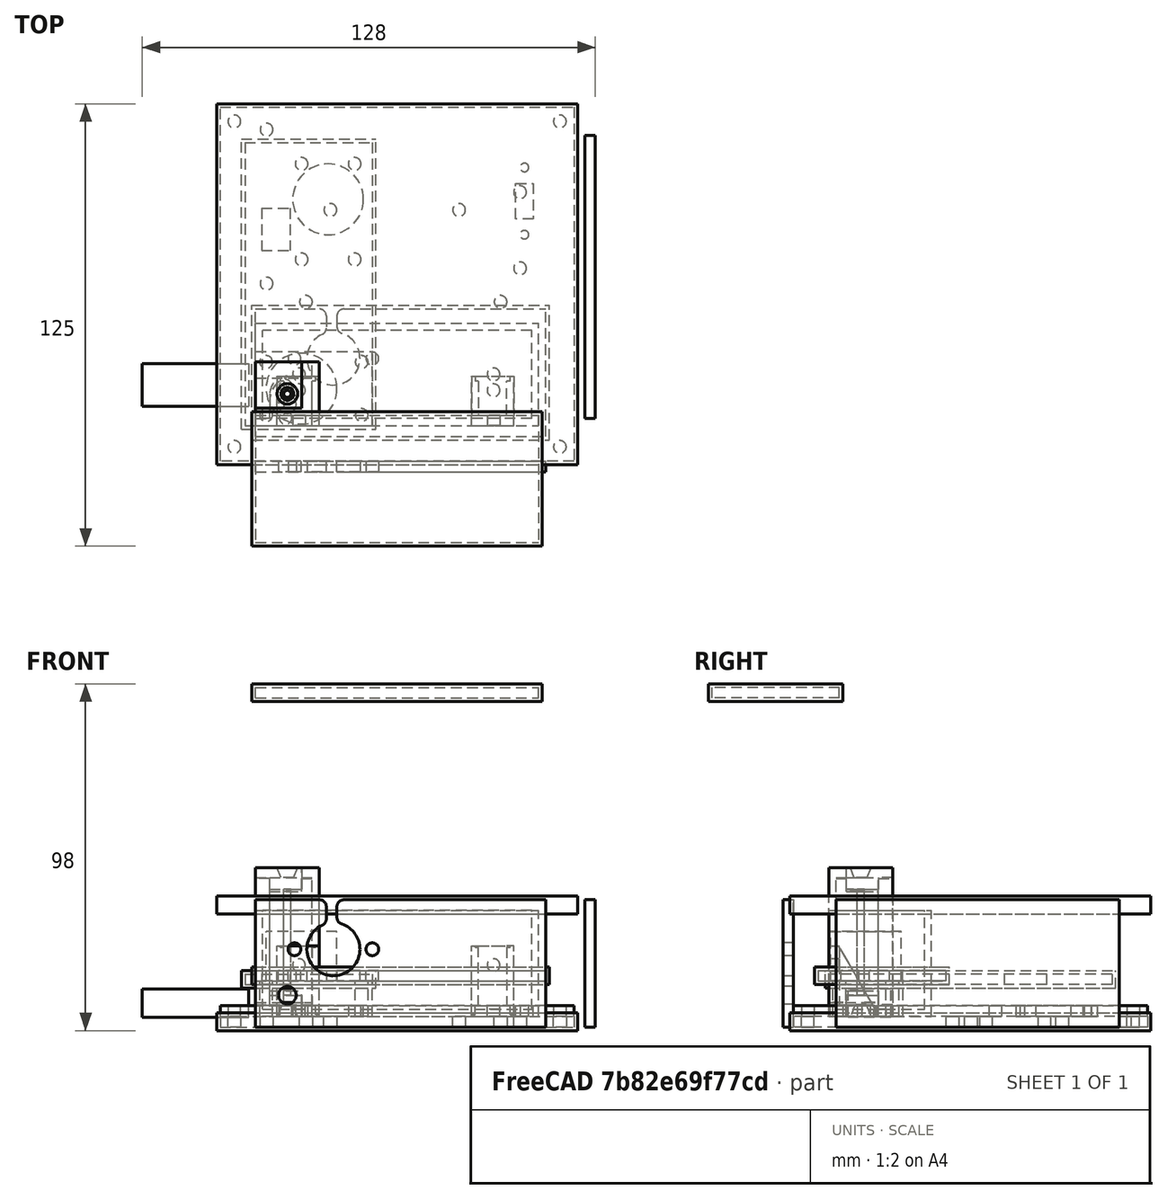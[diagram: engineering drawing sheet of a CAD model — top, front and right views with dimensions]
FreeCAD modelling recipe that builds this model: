
FCSTD DOCUMENT  (FreeCAD 0.19R)
Label: MQsensors
License: All rights reserved
LicenseURL: http://en.wikipedia.org/wiki/All_rights_reserved
objects: Part::Box×23, Part::FeaturePython×18, Path::FeaturePython×15, App::Part×14, Part::Cylinder×11, App::DocumentObjectGroup×10, Part::Cut×9, PartDesign::Body×8, Part::MultiFuse×7, PartDesign::FeatureBase×6, App::FeaturePython×5, Path::FeatureCompoundPython×5, Mesh::Feature×4, Part::Cone×4, Part::Fillet×4, Sketcher::SketchObject×3, PartDesign::Pad×3, PartDesign::Plane×1
note: 100 computed .brp shape members not serialized (recipe doc carries the construction recipe); baked Part::Feature solids carry a one-line shape summary decoded from their .brp

FEATURE [Mesh::Feature] esp8266_201
  Placement = pos=(25,43,0) rot=(0,0,1;0rad)
FEATURE [Mesh::Feature] step_down_12_1_8v  label="step_down_12-1.8v"
  Placement = pos=(63,62,-1e-16) rot=(0,0,1;4.71239rad)
FEATURE [Part::Box] Box  label="Cube"
  AttacherType = Attacher::AttachEngine3D
  Height = 30
  Length = 80
  Width = 29
FEATURE [Part::Box] Box001  label="Cube001"
  AttacherType = Attacher::AttachEngine3D
  Height = 30
  Length = 76
  Placement = pos=(2,2,2) rot=(0,0,-1;0rad)
  Width = 25
FEATURE [Part::Cylinder] Cylinder
  Angle = 360
  AttacherType = Attacher::AttachEngine3D
  Height = 50
  Placement = pos=(12.25,14.5,-10) rot=(0,0,1;0rad)
  Radius = 1.8
FEATURE [Part::FeaturePython] Array  # Draft array (typed FeaturePython)
  Angle = 360
  ArrayType = 0
  Axis = (0,0,1)
  Base = -> Cylinder
  Center = (0,0,0)
  Fuse = false
  IntervalAxis = (0,0,0)
  IntervalX = (55,0,0)
  IntervalY = (0,1,0)
  IntervalZ = (0,0,1)
  NumberPolar = 1
  NumberX = 2
  NumberY = 1
  NumberZ = 1
FEATURE [Part::MultiFuse] Fusion
  Shapes = -> [Box001,Array]
FEATURE [Part::Cut] Cut
  Base = -> Box
  Tool = -> Fusion
FEATURE [App::Part] Part  label="battery mockup"
  Group = -> [Box001,Box,Cut,Cylinder,Array,Fusion]
  Origin = -> Origin
  Placement = pos=(2,25,-5.6e-15) rot=(1,0,0;1.5708rad)
FEATURE [Part::Box] Box002  label="Cube002"
  AttacherType = Attacher::AttachEngine3D
  Height = 4
  Length = 16
  Width = 13.5
FEATURE [Part::Cylinder] Cylinder001
  Angle = 360
  AttacherType = Attacher::AttachEngine3D
  Height = 50
  Placement = pos=(8.5,2.25,-10) rot=(0,0,1;0rad)
  Radius = 1.8
FEATURE [Part::FeaturePython] Array001  # Draft array (typed FeaturePython)
  Angle = 360
  ArrayType = 0
  Axis = (0,0,1)
  Base = -> Cylinder001
  Center = (0,0,0)
  Fuse = false
  IntervalAxis = (0,0,0)
  IntervalX = (1,0,0)
  IntervalY = (0,9,0)
  IntervalZ = (0,0,1)
  NumberPolar = 1
  NumberX = 1
  NumberY = 2
  NumberZ = 1
FEATURE [Part::Box] Box003  label="Cube003"
  AttacherType = Attacher::AttachEngine3D
  Height = 10
  Length = 33
  Width = 21
FEATURE [Part::Cylinder] Cylinder002
  Angle = 360
  AttacherType = Attacher::AttachEngine3D
  Height = 50
  Placement = pos=(3,3,-10) rot=(0,0,1;0rad)
  Radius = 1.8
FEATURE [Part::FeaturePython] Array002  # Draft array (typed FeaturePython)
  Angle = 360
  ArrayType = 0
  Axis = (0,0,1)
  Base = -> Cylinder002
  Center = (0,0,0)
  Fuse = false
  IntervalAxis = (0,0,0)
  IntervalX = (27,0,0)
  IntervalY = (0,15,0)
  IntervalZ = (0,0,1)
  NumberPolar = 1
  NumberX = 2
  NumberY = 2
  NumberZ = 1
FEATURE [Part::Cut] Cut002
  Base = -> Box003
  Tool = -> Array002
FEATURE [Part::Cylinder] Cylinder003
  Angle = 360
  AttacherType = Attacher::AttachEngine3D
  Height = 14
  Placement = pos=(13,10.5,10) rot=(0,0,1;0rad)
  Radius = 10
FEATURE [App::Part] Part002  label="sensor mockup"
  Group = -> [Box003,Cylinder002,Array002,Cut002,Cylinder003]
  Origin = -> Origin002
  Placement = pos=(10,77,19) rot=(0,0,1;4.71239rad)
FEATURE [Mesh::Feature] switch_mockup_plate
  Placement = pos=(75.3409,-19.717,22) rot=(0,0,-1;4.71239rad)
FEATURE [Part::Box] Box004  label="Cube004"
  AttacherType = Attacher::AttachEngine3D
  Height = 20
  Length = 10
  Placement = pos=(7,0,0) rot=(0,0,1;0rad)
  Width = 3
FEATURE [Part::Box] Box005  label="Cube005"
  AttacherType = Attacher::AttachEngine3D
  Height = 3
  Length = 10
  Placement = pos=(7,2,0) rot=(0,0,1;0rad)
  Width = 12
FEATURE [Part::Cylinder] Cylinder004
  Angle = 360
  AttacherType = Attacher::AttachEngine3D
  Height = 40
  Placement = pos=(12.25,10,14.5) rot=(1,0,0;1.5708rad)
  Radius = 1.8
FEATURE [Part::Cylinder] Cylinder005
  Angle = 360
  AttacherType = Attacher::AttachEngine3D
  Height = 50
  Placement = pos=(12.25,10,-21) rot=(0,0,1;0rad)
  Radius = 1.8
FEATURE [Part::MultiFuse] Fusion002
  Shapes = -> [Cylinder005,Cylinder004]
FEATURE [Part::Box] Box006  label="Cube006"
  AttacherType = Attacher::AttachEngine3D
  Height = 20
  Length = 2
  Placement = pos=(6,0,0) rot=(0,0,1;0rad)
  Width = 14
FEATURE [Part::Box] Box007  label="Cube007"
  AttacherType = Attacher::AttachEngine3D
  Height = 40
  Length = 2
  Placement = pos=(6,16.3978,-3.62848) rot=(1,0,0;0.523599rad)
  Width = 20
FEATURE [Part::Cut] Cut004
  Base = -> Box006
  Tool = -> Box007
FEATURE [Part::FeaturePython] Array004  # Draft array (typed FeaturePython)
  Angle = 360
  ArrayType = 0
  Axis = (0,0,1)
  Base = -> Cut004
  Center = (0,0,0)
  Fuse = false
  IntervalAxis = (0,0,0)
  IntervalX = (10,0,0)
  IntervalY = (0,1,0)
  IntervalZ = (0,0,1)
  NumberPolar = 1
  NumberX = 2
  NumberY = 0
  NumberZ = 1
FEATURE [Part::MultiFuse] Fusion001
  Shapes = -> [Box004,Box005,Array004]
FEATURE [Part::Cut] Cut003
  Base = -> Fusion001
  Tool = -> Fusion002
FEATURE [Part::FeaturePython] Array003  # Draft array (typed FeaturePython)
  Angle = 360
  ArrayType = 0
  Axis = (0,0,1)
  Base = -> Cut003
  Center = (0,0,0)
  Fuse = false
  IntervalAxis = (0,0,0)
  IntervalX = (55,0,0)
  IntervalY = (0,1,0)
  IntervalZ = (0,0,1)
  NumberPolar = 1
  NumberX = 2
  NumberY = 1
  NumberZ = 1
FEATURE [App::Part] Part003  label="battery holder brackets"
  Group = -> [Box005,Array003,Box004,Fusion001,Cylinder004,Cylinder005,Fusion002,Cut003,Box006,Box007,Cut004,Array004]
  Origin = -> Origin003
  Placement = pos=(2,25,0) rot=(0,0,1;0rad)
FEATURE [PartDesign::Plane] DatumPlane
  Length = 138
  MapMode = 5
  ResizeMode = 0
  Support = -> [XY_Plane004]
  Width = 138
FEATURE [Sketcher::SketchObject] Sketch
  FullyConstrained = false
  MapMode = 5
  Support = -> [DatumPlane]
  sketch-geometry (16):
    g0: LineSegment StartX=-10 StartY=90 StartZ=0 EndX=90 EndY=90 EndZ=0
    g1: LineSegment StartX=90 StartY=90 StartZ=0 EndX=90 EndY=-10 EndZ=0
    g2: LineSegment StartX=90 StartY=-10 StartZ=0 EndX=-10 EndY=-10 EndZ=0
    g3: LineSegment StartX=-10 StartY=-10 StartZ=0 EndX=-10 EndY=90 EndZ=0
    g4: Circle CenterX=3.12 CenterY=83.7 CenterZ=0 NormalX=0 NormalY=0 NormalZ=1 AngleXU=0 Radius=1.8
    g5: Circle CenterX=3.12 CenterY=40.2 CenterZ=0 NormalX=0 NormalY=0 NormalZ=1 AngleXU=0 Radius=1.8
    g6: Circle CenterX=14.25 CenterY=35 CenterZ=0 NormalX=0 NormalY=0 NormalZ=1 AngleXU=0 Radius=1.8
    g7: Circle CenterX=69.25 CenterY=35 CenterZ=0 NormalX=0 NormalY=0 NormalZ=1 AngleXU=0 Radius=1.8
    g8: Circle CenterX=74.74 CenterY=66 CenterZ=0 NormalX=0 NormalY=0 NormalZ=1 AngleXU=0 Radius=1.8
    g9: Circle CenterX=74.74 CenterY=44.5 CenterZ=0 NormalX=0 NormalY=0 NormalZ=1 AngleXU=0 Radius=1.8
    g10: Circle CenterX=21.13 CenterY=61 CenterZ=0 NormalX=0 NormalY=0 NormalZ=1 AngleXU=0 Radius=1.8
    g11: Circle CenterX=57.53 CenterY=61 CenterZ=0 NormalX=0 NormalY=0 NormalZ=1 AngleXU=0 Radius=1.8
    g12: Circle CenterX=-6 CenterY=86 CenterZ=0 NormalX=0 NormalY=0 NormalZ=1 AngleXU=0 Radius=1.8
    g13: Circle CenterX=86 CenterY=86 CenterZ=0 NormalX=0 NormalY=0 NormalZ=1 AngleXU=0 Radius=1.8
    g14: Circle CenterX=-6 CenterY=-6 CenterZ=0 NormalX=0 NormalY=0 NormalZ=1 AngleXU=0 Radius=1.8
    g15: Circle CenterX=86 CenterY=-6 CenterZ=0 NormalX=0 NormalY=0 NormalZ=1 AngleXU=0 Radius=1.8
  constraints (48):
    c: Coincident(g0,g1)
    c: Coincident(g1,g2)
    c: Coincident(g2,g3)
    c: Coincident(g3,g0)
    c: Horizontal(g0)
    c: Horizontal(g2)
    c: Vertical(g1)
    c: Vertical(g3)
    c: Equal(g7,g6)
    c: Equal(g11,g10)
    c: Radius(g11) = 1.8
    c: DistanceY(g10,g11) = 0
    c: DistanceX(g10,g11) = 36.4
    c: Equal(g4,g5)
    c: DistanceY(g6,g7) = 0
    c: DistanceX(g6,g7) = 55
    c: Radius(g6) = 1.8
    c: Equal(g8,g9)
    c: Radius(g8) = 1.8
    c: DistanceX(g8,g9) = 0
    c: DistanceY(g9,g8) = 21.5
    c: DistanceY(g1,g1) = 100
    c: DistanceX(g0,g0) = 100
    c: DistanceX(g2,g-1) = 10
    c: DistanceY(g2,g-1) = 10
    c: DistanceY(g-1,g6) = 35
    c: Radius(g12) = 1.8
    c: Equal(g12,g13)
    c: Equal(g13,g15)
    c: Equal(g15,g14)
    c: DistanceX(g2,g14) = 4
    c: DistanceY(g2,g14) = 4
    c: DistanceY(g15,g14) = 0
    c: DistanceX(g15,g1) = 4
    c: DistanceX(g15,g13) = 0
    c: DistanceY(g13,g0) = 4
    c: DistanceY(g13,g12) = 0
    c: DistanceX(g12,g14) = 0
    c: DistanceY(g-1,g10) = 61
    c: DistanceY(g-1,g9) = 44.5
    c: DistanceX(g-1,g10) = 21.13
    c: DistanceX(g4,g5) = 0
    c: DistanceY(g5,g4) = 43.5
    c: DistanceX(g-1,g5) = 3.12
    c: DistanceY(g-1,g5) = 40.2
    c: DistanceX(g-1,g9) = 74.74
    c: Radius(g4) = 1.8
    c: DistanceX(g-1,g6) = 14.25
FEATURE [Sketcher::SketchObject] Sketch001
  FullyConstrained = false
  sketch-geometry (19):
    g0: LineSegment StartX=-10 StartY=90 StartZ=0 EndX=90 EndY=90 EndZ=0
    g1: LineSegment StartX=90 StartY=90 StartZ=0 EndX=90 EndY=-10 EndZ=0
    g2: LineSegment StartX=90 StartY=-10 StartZ=0 EndX=-10 EndY=-10 EndZ=0
    g3: LineSegment StartX=-10 StartY=-10 StartZ=0 EndX=-10 EndY=90 EndZ=0
    g4: Circle CenterX=76 CenterY=73 CenterZ=0 NormalX=0 NormalY=0 NormalZ=1 AngleXU=0 Radius=1.2
    g5: Circle CenterX=76 CenterY=54 CenterZ=0 NormalX=0 NormalY=0 NormalZ=1 AngleXU=0 Radius=1.2
    g6: Circle CenterX=28 CenterY=47 CenterZ=0 NormalX=0 NormalY=0 NormalZ=1 AngleXU=0 Radius=1.8
    g7: Circle CenterX=13 CenterY=47 CenterZ=0 NormalX=0 NormalY=0 NormalZ=1 AngleXU=0 Radius=1.8
    g8: Circle CenterX=13 CenterY=74 CenterZ=0 NormalX=0 NormalY=0 NormalZ=1 AngleXU=0 Radius=1.8
    g9: Circle CenterX=28 CenterY=74 CenterZ=0 NormalX=0 NormalY=0 NormalZ=1 AngleXU=0 Radius=1.8
    g10: Circle CenterX=20.5 CenterY=64 CenterZ=0 NormalX=0 NormalY=0 NormalZ=1 AngleXU=0 Radius=10
    g11: LineSegment StartX=78.5 StartY=58.5 StartZ=0 EndX=73.5 EndY=58.5 EndZ=0
    g12: LineSegment StartX=73.5 StartY=58.5 StartZ=0 EndX=73.5 EndY=68.5 EndZ=0
    g13: LineSegment StartX=73.5 StartY=68.5 StartZ=0 EndX=78.5 EndY=68.5 EndZ=0
    g14: LineSegment StartX=78.5 StartY=68.5 StartZ=0 EndX=78.5 EndY=58.5 EndZ=0
    g15: Circle CenterX=-6 CenterY=86 CenterZ=0 NormalX=0 NormalY=0 NormalZ=1 AngleXU=0 Radius=1.8
    g16: Circle CenterX=86 CenterY=86 CenterZ=0 NormalX=0 NormalY=0 NormalZ=1 AngleXU=0 Radius=1.8
    g17: Circle CenterX=-6 CenterY=-6 CenterZ=0 NormalX=0 NormalY=0 NormalZ=1 AngleXU=0 Radius=1.8
    g18: Circle CenterX=86 CenterY=-6 CenterZ=0 NormalX=0 NormalY=0 NormalZ=1 AngleXU=0 Radius=1.8
  constraints (57):
    c: Coincident(g0,g1)
    c: Coincident(g1,g2)
    c: Coincident(g2,g3)
    c: Coincident(g3,g0)
    c: Horizontal(g0)
    c: Horizontal(g2)
    c: Vertical(g1)
    c: Vertical(g3)
    c: Coincident(g11,g12)
    c: Coincident(g12,g13)
    c: Coincident(g13,g14)
    c: Coincident(g14,g11)
    c: Horizontal(g11)
    c: Horizontal(g13)
    c: Vertical(g12)
    c: Vertical(g14)
    c: DistanceY(g8,g9) = 0
    c: DistanceY(g6,g7) = 0
    c: DistanceX(g9,g6) = 0
    c: Radius(g7) = 1.8
    c: Equal(g7,g6)
    c: Equal(g6,g9)
    c: Equal(g9,g8)
    c: DistanceY(g6,g9) = 27
    c: DistanceX(g7,g6) = 15
    c: Radius(g5) = 1.2
    c: Equal(g4,g5)
    c: DistanceY(g1,g1) = 100
    c: DistanceX(g0,g0) = 100
    c: DistanceX(g11,g11) = 5
    c: DistanceY(g12,g12) = 10
    c: DistanceX(g2,g-1) = 10
    c: DistanceY(g2,g-1) = 10
    c: Radius(g10) = 10
    c: DistanceX(g7,g10) = 7.5
    c: DistanceY(g10,g8) = 10
    c: DistanceX(g7,g8) = 0
    c: Radius(g15) = 1.8
    c: Equal(g15,g16)
    c: Equal(g16,g18)
    c: Equal(g18,g17)
    c: DistanceX(g2,g17) = 4
    c: DistanceY(g2,g17) = 4
    c: DistanceY(g18,g17) = 0
    c: DistanceX(g18,g1) = 4
    c: DistanceX(g18,g16) = 0
    c: DistanceY(g16,g0) = 4
    c: DistanceY(g16,g15) = 0
    c: DistanceX(g15,g17) = 0
    c: DistanceX(g-1,g7) = 13
    c: DistanceX(g5,g4) = 0
    c: DistanceY(g5,g4) = 19
    c: DistanceX(g12,g4) = 2.5
    c: DistanceY(g12,g4) = 4.5
    c: DistanceX(g17,g5) = 82
    c: DistanceY(g17,g5) = 60
    c: DistanceY(g-1,g7) = 47
FEATURE [PartDesign::Pad] Pad001
  AllowMultiFace = false
  Direction = (1,1,1)
  Length = 3
  Length2 = 100
  Profile = -> Sketch001
  Type = 0
FEATURE [PartDesign::Body] Body001  label="top plate"
  Group = -> [Sketch001,Pad001]
  Origin = -> Origin007
  Tip = -> Pad001
FEATURE [App::Part] Part005  label="top plate part"
  Group = -> [Body001]
  Origin = -> Origin006
  Placement = pos=(0,0,30) rot=(0,0,1;0rad)
FEATURE [PartDesign::Pad] Pad
  AllowMultiFace = false
  Direction = (1,1,1)
  Length = 3
  Length2 = 100
  Profile = -> Sketch
  Reversed = true
  Type = 0
FEATURE [PartDesign::Body] Body  label="bottom plate"
  Group = -> [DatumPlane,Sketch,Pad]
  Origin = -> Origin004
  Tip = -> Pad
FEATURE [App::Part] Part004  label="bottom plate part"
  Group = -> [Body]
  Origin = -> Origin005
FEATURE [Mesh::Feature] lion_manager
  Placement = pos=(0,0,0) rot=(0,0,1;1.5708rad)
FEATURE [Part::Cut] Cut001
  Base = -> Box002
  Tool = -> Array001
FEATURE [App::Part] Part001  label="micro usb mockup"
  Group = -> [Box002,Cylinder001,Array001,Cut001]
  Origin = -> Origin001
  Placement = pos=(63,87,0) rot=(0,0,1;4.71239rad)
FEATURE [App::FeaturePython] SetupSheet  # Path/CAM operation (typed FeaturePython)
  ClearanceHeightExpression = OpStockZMax+SetupSheet.ClearanceHeightOffset
  ClearanceHeightOffset = 0
  CoolantMode = 0
  CoolantModes = None | Flood | Mist
  FinalDepthExpression = OpFinalDepth
  HorizRapid = 10
  SafeHeightExpression = OpStockZMax+SetupSheet.SafeHeightOffset
  SafeHeightOffset = 0
  StartDepthExpression = OpStartDepth
  StepDownExpression = OpToolDiameter
  VertRapid = 10
FEATURE [Part::FeaturePython] Clone  label="Model-bottom plate part"  # Draft clone (typed FeaturePython)
  AttacherType = Attacher::AttachEngine3D
  Fuse = false
  Objects = -> [Part004]
  PathResource = Model
  Scale = (1,1,1)
FEATURE [App::DocumentObjectGroup] Model
  Group = -> [Clone]
FEATURE [Part::FeaturePython] Stock  # WARN: FeaturePython — macro-defined, semantics opaque (R4)
  Base = -> Model
  ExtXneg = 1
  ExtXpos = 1
  ExtYneg = 1
  ExtYpos = 1
  ExtZneg = 1
  ExtZpos = 1
  Placement = pos=(-10,-10,-3) rot=(0,0,1;0rad)
  StockType = FromBase
FEATURE [Path::FeaturePython] T3__laser  label="T3: laser"  # Path/CAM operation (typed FeaturePython)
  HorizFeed = 1
  HorizRapid = 10
  SpindleDir = 0
  SpindleSpeed = 1000
  ToolNumber = 3
  VertFeed = 1
  VertRapid = 10
  expr: HorizRapid = SetupSheet.HorizRapid
  expr: VertRapid = SetupSheet.VertRapid
FEATURE [Path::FeaturePython] Engrave  # Path/CAM operation (typed FeaturePython)
  Active = true
  Base = -> [Clone]
  ClearanceHeight = 1
  FinalDepth = 0
  OpFinalDepth = -0.2
  OpStartDepth = 0
  OpStockZMax = 1
  OpStockZMin = -4
  OpToolDiameter = 0.2
  SafeHeight = 1
  StartDepth = 0
  StartVertex = 0
  StepDown = 0.2
  ToolController = -> T3__laser
  expr: ClearanceHeight = OpStockZMax + SetupSheet.ClearanceHeightOffset
  expr: SafeHeight = OpStockZMax + SetupSheet.SafeHeightOffset
  expr: StepDown = OpToolDiameter
  expr: StartDepth = OpStartDepth
FEATURE [Path::FeatureCompoundPython] Operations  # Path/CAM operation (typed FeaturePython)
  Group = -> [Engrave]
  UsePlacements = false
FEATURE [App::FeaturePython] SetupSheet001  # Path/CAM operation (typed FeaturePython)
  ClearanceHeightExpression = OpStockZMax+SetupSheet001.ClearanceHeightOffset
  ClearanceHeightOffset = 0
  CoolantMode = 0
  CoolantModes = None | Flood | Mist
  FinalDepthExpression = OpFinalDepth
  HorizRapid = 10
  SafeHeightExpression = OpStockZMax+SetupSheet001.SafeHeightOffset
  SafeHeightOffset = 0
  StartDepthExpression = OpStartDepth
  StepDownExpression = OpToolDiameter
  VertRapid = 10
FEATURE [Part::FeaturePython] Clone001  label="Model-top plate part"  # Draft clone (typed FeaturePython)
  AttacherType = Attacher::AttachEngine3D
  Fuse = false
  Objects = -> [Part005]
  PathResource = Model
  Scale = (1,1,1)
FEATURE [App::DocumentObjectGroup] Model001
  Group = -> [Clone001]
FEATURE [Part::FeaturePython] Stock001  # WARN: FeaturePython — macro-defined, semantics opaque (R4)
  Base = -> Model001
  ExtXneg = 1
  ExtXpos = 1
  ExtYneg = 1
  ExtYpos = 1
  ExtZneg = 1
  ExtZpos = 1
  Placement = pos=(-10,-10,30) rot=(0,0,1;0rad)
  StockType = FromBase
FEATURE [Path::FeaturePython] T3__laser001  label="T3: laser001"  # Path/CAM operation (typed FeaturePython)
  HorizFeed = 0.6
  HorizRapid = 10
  SpindleDir = 0
  SpindleSpeed = 1000
  ToolNumber = 3
  VertFeed = 0.6
  VertRapid = 10
  expr: HorizRapid = SetupSheet001.HorizRapid
  expr: VertRapid = SetupSheet001.VertRapid
FEATURE [Path::FeaturePython] Engrave001  # Path/CAM operation (typed FeaturePython)
  Active = true
  Base = -> [Clone001]
  ClearanceHeight = 34
  FinalDepth = 0
  OpFinalDepth = 2.8
  OpStartDepth = 3
  OpStockZMax = 34
  OpStockZMin = 29
  OpToolDiameter = 0.2
  SafeHeight = 34
  StartDepth = 0
  StartVertex = 0
  StepDown = 0.2
  ToolController = -> T3__laser001
  expr: ClearanceHeight = OpStockZMax + SetupSheet001.ClearanceHeightOffset
  expr: SafeHeight = OpStockZMax + SetupSheet001.SafeHeightOffset
  expr: StepDown = OpToolDiameter
FEATURE [Path::FeatureCompoundPython] Operations001  # Path/CAM operation (typed FeaturePython)
  Group = -> [Engrave001]
  UsePlacements = false
FEATURE [Part::Box] Box008  label="Cube008"
  AttacherType = Attacher::AttachEngine3D
  Height = 36
  Length = 82
  Placement = pos=(0,-13,-3) rot=(0,0,1;0rad)
  Width = 3
FEATURE [Part::Box] Box009  label="plane wall cube"
  AttacherType = Attacher::AttachEngine3D
  Height = 36
  Length = 80
  Placement = pos=(0,90,-3) rot=(0,0,1;0rad)
  Width = 3
FEATURE [Part::Box] Box010  label="Cube010"
  AttacherType = Attacher::AttachEngine3D
  Height = 42
  Length = 18
  Width = 18
FEATURE [Part::Box] Box011  label="Cube011"
  AttacherType = Attacher::AttachEngine3D
  Height = 4
  Length = 18
  Placement = pos=(-5,5,3.3) rot=(0,0,1;0rad)
  Width = 18
FEATURE [Part::Box] Box012  label="Cube012"
  AttacherType = Attacher::AttachEngine3D
  Height = 36
  Length = 18
  Placement = pos=(-14,2,3.3) rot=(0,0,1;0rad)
  Width = 18
FEATURE [Part::Box] Box013  label="Cube013"
  AttacherType = Attacher::AttachEngine3D
  Height = 36
  Length = 18
  Placement = pos=(-2,14,3.3) rot=(0,0,1;0rad)
  Width = 18
FEATURE [Part::Cylinder] Cylinder006
  Angle = 360
  AttacherType = Attacher::AttachEngine3D
  Height = 70
  Placement = pos=(9,9,-17) rot=(0,0,1;0rad)
  Radius = 1
FEATURE [Part::FeaturePython] Array005  # Draft array (typed FeaturePython)
  Angle = 360
  ArrayType = 0
  Axis = (0,0,1)
  Base = -> Box011
  Center = (0,0,0)
  Fuse = false
  IntervalAxis = (0,0,0)
  IntervalX = (1,0,0)
  IntervalY = (0,1,0)
  IntervalZ = (0,0,32)
  NumberPolar = 1
  NumberX = 1
  NumberY = 1
  NumberZ = 2
FEATURE [Part::Cone] Cone
  Angle = 360
  AttacherType = Attacher::AttachEngine3D
  Height = 3.5
  Placement = pos=(9,9,0) rot=(0,0,1;0rad)
  Radius1 = 2.9
  Radius2 = 1.5
FEATURE [Part::Cone] Cone001
  Angle = 360
  AttacherType = Attacher::AttachEngine3D
  Height = 3.5
  Placement = pos=(9,9,38.5) rot=(0,0,1;0rad)
  Radius1 = 1.5
  Radius2 = 2.9
FEATURE [Part::MultiFuse] Fusion003
  Shapes = -> [Box012,Box013,Cylinder006,Array005,Cone,Cone001]
FEATURE [Part::Cut] Cut005
  Base = -> Box010
  Tool = -> Fusion003
FEATURE [Part::Fillet] Fillet
  Base = -> Cut005
  Edges = 1 edges r=5: [Edge58]
FEATURE [App::Part] Part007  label="corner part"
  Group = -> [Box010,Box012,Box013,Fusion003,Cut005,Cylinder006,Box011,Array005,Cone,Cone001,Fillet]
  Origin = -> Origin009
  Placement = pos=(77,-15,-6.3) rot=(0,0,1;0rad)
FEATURE [PartDesign::FeatureBase] Clone002
  BaseFeature = -> Fillet
FEATURE [PartDesign::Body] Body002  label="corner clone"
  BaseFeature = -> Fillet
  Group = -> [Clone002]
  Origin = -> Origin010
  Tip = -> Clone002
FEATURE [App::Part] Part008  label="corner clone part"
  Group = -> [Body002]
  Origin = -> Origin011
  Placement = pos=(-15,3,-6) rot=(0,0,1;4.71239rad)
FEATURE [Part::Cylinder] Cylinder007
  Angle = 360
  AttacherType = Attacher::AttachEngine3D
  Height = 23
  Radius = 7.5
FEATURE [Part::Cylinder] Cylinder008
  Angle = 360
  AttacherType = Attacher::AttachEngine3D
  Height = 10
  Placement = pos=(-11,0,0) rot=(0,0,1;0rad)
  Radius = 1.8
FEATURE [Part::FeaturePython] Array006  # Draft array (typed FeaturePython)
  Angle = 360
  ArrayType = 0
  Axis = (0,0,1)
  Base = -> Cylinder008
  Center = (0,0,0)
  Fuse = false
  IntervalAxis = (0,0,0)
  IntervalX = (22,0,0)
  IntervalY = (0,1,0)
  IntervalZ = (0,0,1)
  NumberPolar = 1
  NumberX = 2
  NumberY = 0
  NumberZ = 1
FEATURE [Part::MultiFuse] Fusion004  label="tape recorder socket mockup"
  Shapes = -> [Cylinder007,Array006]
FEATURE [App::Part] Part009  label="tape recorder socket mockup part"
  Group = -> [Array006,Cylinder008,Cylinder007,Fusion004]
  Origin = -> Origin012
FEATURE [PartDesign::FeatureBase] Clone003  label="tape recorder socket clone"
  BaseFeature = -> Fusion004
  Placement = pos=(22,-4,19) rot=(1,0,0;1.5708rad)
FEATURE [Part::Cylinder] Cylinder009  label="led hole"
  Angle = 360
  AttacherType = Attacher::AttachEngine3D
  Height = 50
  Placement = pos=(0,0,0) rot=(1,0,0;1.5708rad)
  Radius = 2.5
FEATURE [App::Part] Part010  label="led mockup part"
  Origin = -> Origin014
FEATURE [PartDesign::FeatureBase] Clone004
  BaseFeature = -> Cylinder009
  Placement = pos=(0,0,0) rot=(1,0,0;1.5708rad)
FEATURE [PartDesign::Body] Body004  label="led hole clone body"
  BaseFeature = -> Cylinder009
  Group = -> [Clone004]
  Origin = -> Origin015
  Placement = pos=(9,16,6) rot=(0,0,1;0rad)
  Tip = -> Clone004
FEATURE [Part::Box] Box014  label="Cube014"
  AttacherType = Attacher::AttachEngine3D
  Height = 42
  Length = 18
  Width = 18
FEATURE [Part::Box] Box015  label="Cube015"
  AttacherType = Attacher::AttachEngine3D
  Height = 6
  Length = 18
  Placement = pos=(-5,5,0) rot=(0,0,1;0rad)
  Width = 18
FEATURE [Part::Box] Box016  label="Cube016"
  AttacherType = Attacher::AttachEngine3D
  Height = 36
  Length = 18
  Placement = pos=(-14,2,3) rot=(0,0,1;0rad)
  Width = 18
FEATURE [Part::Box] Box017  label="Cube017"
  AttacherType = Attacher::AttachEngine3D
  Height = 36
  Length = 18
  Placement = pos=(-2,14,3) rot=(0,0,1;0rad)
  Width = 18
FEATURE [Part::Cylinder] Cylinder010
  Angle = 360
  AttacherType = Attacher::AttachEngine3D
  Height = 70
  Placement = pos=(9,9,-17) rot=(0,0,1;0rad)
  Radius = 1
FEATURE [Part::FeaturePython] Array007  # Draft array (typed FeaturePython)
  Angle = 360
  ArrayType = 0
  Axis = (0,0,1)
  Base = -> Box015
  Center = (0,0,0)
  Fuse = false
  IntervalAxis = (0,0,0)
  IntervalX = (1,0,0)
  IntervalY = (0,1,0)
  IntervalZ = (0,0,36)
  NumberPolar = 1
  NumberX = 1
  NumberY = 1
  NumberZ = 2
FEATURE [Part::Cone] Cone002
  Angle = 360
  AttacherType = Attacher::AttachEngine3D
  Height = 3.5
  Placement = pos=(9,9,0) rot=(0,0,1;0rad)
  Radius1 = 2.9
  Radius2 = 1.5
FEATURE [Part::Cone] Cone003
  Angle = 360
  AttacherType = Attacher::AttachEngine3D
  Height = 3.5
  Placement = pos=(9,9,38.5) rot=(0,0,1;0rad)
  Radius1 = 1.5
  Radius2 = 2.9
FEATURE [Part::MultiFuse] Fusion006
  Shapes = -> [Box016,Box017,Cylinder010,Array007,Cone002,Cone003]
FEATURE [Part::Cut] Cut007
  Base = -> Box014
  Tool = -> Fusion006
FEATURE [Part::Fillet] Fillet001
  Base = -> Cut007
  Edges = 1 edges r=7: [Edge45]
FEATURE [App::Part] Part011  label="corner part v2"
  Group = -> [Box014,Box016,Box017,Fusion006,Cut007,Cylinder010,Box015,Array007,Cone002,Cone003,Fillet001]
  Origin = -> Origin016
  Placement = pos=(77,-15,-6) rot=(0,0,1;0rad)
FEATURE [Part::Box] Box018  label="plane wall cube 1"
  AttacherType = Attacher::AttachEngine3D
  Height = 36
  Length = 80
  Placement = pos=(93,82,-3) rot=(0,0,-1;1.5708rad)
  Width = 3
FEATURE [Part::Box] Box019  label="Cube019"
  AttacherType = Attacher::AttachEngine3D
  Height = 36
  Length = 80
  Placement = pos=(0,0,0) rot=(0,0,-1;1.5708rad)
  Width = 3
FEATURE [Part::Box] Box020  label="micro usb hole"
  AttacherType = Attacher::AttachEngine3D
  Height = 8
  Length = 12
  Placement = pos=(3.9e-15,-18.5,4.7) rot=(0,0,-1;1.5708rad)
  Width = 30
FEATURE [Part::Cut] Cut008  label="wall with micro usb hole"
  Base = -> Box019
  Placement = pos=(-12,80,-3) rot=(0,0,1;0rad)
  Tool = -> Box020
FEATURE [App::FeaturePython] SetupSheet002  # Path/CAM operation (typed FeaturePython)
  ClearanceHeightExpression = OpStockZMax+SetupSheet002.ClearanceHeightOffset
  ClearanceHeightOffset = 0
  CoolantMode = 0
  CoolantModes = None | Flood | Mist
  FinalDepthExpression = OpFinalDepth
  HorizRapid = 10
  SafeHeightExpression = OpStockZMax+SetupSheet002.SafeHeightOffset
  SafeHeightOffset = 0
  StartDepthExpression = OpStartDepth
  StepDownExpression = OpToolDiameter
  VertRapid = 10
FEATURE [Path::FeaturePython] T3__laser002  label="T3: laser002"  # Path/CAM operation (typed FeaturePython)
  HorizFeed = 0.5
  HorizRapid = 10
  SpindleDir = 0
  SpindleSpeed = 1000
  ToolNumber = 3
  VertFeed = 0.5
  VertRapid = 10
  expr: HorizRapid = SetupSheet002.HorizRapid
  expr: VertRapid = SetupSheet002.VertRapid
FEATURE [PartDesign::FeatureBase] Clone008
  BaseFeature = -> Box009
  Placement = pos=(0,90,-3) rot=(0,0,1;0rad)
FEATURE [PartDesign::Body] Body006  label="plain wall clone body"
  BaseFeature = -> Box009
  Group = -> [Clone008]
  Origin = -> Origin020
  Placement = pos=(0,0,0) rot=(1,0,0;1.5708rad)
  Tip = -> Clone008
FEATURE [App::FeaturePython] SetupSheet003  # Path/CAM operation (typed FeaturePython)
  ClearanceHeightExpression = OpStockZMax+SetupSheet003.ClearanceHeightOffset
  ClearanceHeightOffset = 0
  CoolantMode = 0
  CoolantModes = None | Flood | Mist
  FinalDepthExpression = OpFinalDepth
  HorizRapid = 100
  SafeHeightExpression = OpStockZMax+SetupSheet003.SafeHeightOffset
  SafeHeightOffset = 0
  StartDepthExpression = OpStartDepth
  StepDownExpression = OpToolDiameter
  VertRapid = 100
FEATURE [Part::FeaturePython] Clone009  label="Model-plain wall body"  # Draft clone (typed FeaturePython)
  AttacherType = Attacher::AttachEngine3D
  Fuse = false
  Objects = -> [Body006]
  PathResource = Model
  Placement = pos=(0,0,0) rot=(1,0,0;1.5708rad)
  Scale = (1,1,1)
FEATURE [App::DocumentObjectGroup] Model003
  Group = -> [Clone009]
FEATURE [Part::FeaturePython] Stock003  # WARN: FeaturePython — macro-defined, semantics opaque (R4)
  Base = -> Model003
  ExtXneg = 1
  ExtXpos = 1
  ExtYneg = 1
  ExtYpos = 1
  ExtZneg = 1
  ExtZpos = 1
  Placement = pos=(0,-33,90) rot=(0,0,1;0rad)
  StockType = FromBase
FEATURE [Path::FeaturePython] T3__laser003  label="T3: laser003"  # Path/CAM operation (typed FeaturePython)
  HorizFeed = 0.5
  HorizRapid = 100
  SpindleDir = 0
  SpindleSpeed = 1000
  ToolNumber = 3
  VertFeed = 0.5
  VertRapid = 100
  expr: HorizRapid = SetupSheet003.HorizRapid
  expr: VertRapid = SetupSheet003.VertRapid
FEATURE [Path::FeaturePython] Engrave003  # Path/CAM operation (typed FeaturePython)
  Active = true
  Base = -> [Clone009]
  ClearanceHeight = 94
  FinalDepth = 0
  OpFinalDepth = 92.8
  OpStartDepth = 93
  OpStockZMax = 94
  OpStockZMin = 89
  OpToolDiameter = 0.2
  SafeHeight = 94
  StartDepth = 0
  StartVertex = 0
  StepDown = 0.2
  ToolController = -> T3__laser003
  expr: ClearanceHeight = OpStockZMax + SetupSheet003.ClearanceHeightOffset
  expr: SafeHeight = OpStockZMax + SetupSheet003.SafeHeightOffset
  expr: StepDown = OpToolDiameter
FEATURE [Path::FeatureCompoundPython] Operations003  # Path/CAM operation (typed FeaturePython)
  Group = -> [Engrave003]
  UsePlacements = false
FEATURE [Part::Box] Box021  label="micro usb hole001"
  AttacherType = Attacher::AttachEngine3D
  Height = 8
  Length = 12
  Placement = pos=(-32,17.5,-0.2) rot=(0,0,-1;1.5708rad)
  Width = 30
FEATURE [App::Part] Part014  label="lion manager mockup part"
  Group = -> [lion_manager,Box021]
  Origin = -> Origin021
  Placement = pos=(16,44,2) rot=(0,0,1;0rad)
FEATURE [PartDesign::FeatureBase] Clone010
  BaseFeature = -> Cut008
  Placement = pos=(-12,80,-3) rot=(0,0,1;0rad)
FEATURE [PartDesign::Body] Body007  label="wall with micro usb clone"
  BaseFeature = -> Cut008
  Group = -> [Clone010]
  Origin = -> Origin022
  Placement = pos=(0,0,0) rot=(0,1,0;1.5708rad)
  Tip = -> Clone010
FEATURE [App::FeaturePython] SetupSheet004  # Path/CAM operation (typed FeaturePython)
  ClearanceHeightExpression = OpStockZMax+SetupSheet004.ClearanceHeightOffset
  ClearanceHeightOffset = 0
  CoolantMode = 0
  CoolantModes = None | Flood | Mist
  FinalDepthExpression = OpFinalDepth
  HorizRapid = 100
  SafeHeightExpression = OpStockZMax+SetupSheet004.SafeHeightOffset
  SafeHeightOffset = 0
  StartDepthExpression = OpStartDepth
  StepDownExpression = OpToolDiameter
  VertRapid = 100
FEATURE [Part::FeaturePython] Clone011  label="Model-wall with micro usb clone"  # Draft clone (typed FeaturePython)
  AttacherType = Attacher::AttachEngine3D
  Fuse = false
  Objects = -> [Body007]
  PathResource = Model
  Placement = pos=(0,0,0) rot=(0,1,0;1.5708rad)
  Scale = (1,1,1)
FEATURE [App::DocumentObjectGroup] Model004
  Group = -> [Clone011]
FEATURE [Part::FeaturePython] Stock004  # WARN: FeaturePython — macro-defined, semantics opaque (R4)
  Base = -> Model004
  ExtXneg = 1
  ExtXpos = 1
  ExtYneg = 1
  ExtYpos = 1
  ExtZneg = 1
  ExtZpos = 1
  Placement = pos=(-3,-3e-15,9) rot=(0,0,1;0rad)
  StockType = FromBase
FEATURE [Path::FeaturePython] T3__laser004  label="T3: laser004"  # Path/CAM operation (typed FeaturePython)
  HorizFeed = 0.5
  HorizRapid = 100
  SpindleDir = 0
  SpindleSpeed = 1000
  ToolNumber = 3
  VertFeed = 0.5
  VertRapid = 100
  expr: HorizRapid = SetupSheet004.HorizRapid
  expr: VertRapid = SetupSheet004.VertRapid
FEATURE [Path::FeaturePython] Engrave004  # Path/CAM operation (typed FeaturePython)
  Active = true
  Base = -> [Clone011]
  ClearanceHeight = 0
  FinalDepth = 0
  OpFinalDepth = 11.8
  OpStartDepth = 12
  OpStockZMax = 13
  OpStockZMin = 8
  OpToolDiameter = 0.2
  SafeHeight = 0
  StartDepth = 0
  StartVertex = 0
  StepDown = 0.2
  ToolController = -> T3__laser004
  expr: StepDown = OpToolDiameter
FEATURE [Path::FeatureCompoundPython] Operations004  # Path/CAM operation (typed FeaturePython)
  Group = -> [Engrave004]
  UsePlacements = false
FEATURE [Part::Box] Box022  label="cut for wires cube"
  AttacherType = Attacher::AttachEngine3D
  Height = 10
  Length = 3
  Placement = pos=(20,-16,23.5) rot=(0,0,1;0rad)
  Width = 10
FEATURE [Part::MultiFuse] Fusion005
  Shapes = -> [Clone003,Body004,Box022]
FEATURE [Part::Fillet] Fillet002
  Base = -> Fusion005
  Edges = 2 edges r=2: [Edge4,Edge15]
FEATURE [Part::Cut] Cut006  label="wall with socket cut"
  Base = -> Box008
  Tool = -> Fillet002
FEATURE [Part::Fillet] Fillet003  label="wall with socket and wire hole"
  Base = -> Cut006
  Edges = 2 edges r=2: [Edge19,Edge34]
FEATURE [App::Part] Part006  label="wall part"
  Group = -> [Box008,Box009,Clone003,Cut006,Body004,Fusion005,Box018,Box019,Box020,Cut008,Box022,Cylinder009,Fillet002,Fillet003]
  Origin = -> Origin008
FEATURE [PartDesign::FeatureBase] Clone006
  BaseFeature = -> Fillet003
FEATURE [PartDesign::Body] Body005  label="wall with socket clone"
  BaseFeature = -> Fillet003
  Group = -> [Clone006]
  Origin = -> Origin019
  Tip = -> Clone006
FEATURE [App::Part] Part013  label="wall with socket part"
  Group = -> [Body005]
  Origin = -> Origin018
  Placement = pos=(0,0,0) rot=(1,0,0;4.71239rad)
FEATURE [Part::FeaturePython] Clone007  label="Model-wall with socket part"  # Draft clone (typed FeaturePython)
  AttacherType = Attacher::AttachEngine3D
  Fuse = false
  Objects = -> [Part013]
  PathResource = Model
  Placement = pos=(0,0,0) rot=(-1,0,0;1.5708rad)
  Scale = (1,1,1)
FEATURE [App::DocumentObjectGroup] Model002
  Group = -> [Clone007]
FEATURE [Part::FeaturePython] Stock002  # WARN: FeaturePython — macro-defined, semantics opaque (R4)
  Base = -> Model002
  ExtXneg = 1
  ExtXpos = 1
  ExtYneg = 1
  ExtYpos = 1
  ExtZneg = 1
  ExtZpos = 1
  Placement = pos=(0,-3,10) rot=(0,0,1;0rad)
  StockType = FromBase
FEATURE [Path::FeaturePython] Engrave002  # Path/CAM operation (typed FeaturePython)
  Active = true
  Base = -> [Clone007]
  ClearanceHeight = 0
  FinalDepth = 0
  OpFinalDepth = 12.8
  OpStartDepth = 13
  OpStockZMax = 14
  OpStockZMin = 9
  OpToolDiameter = 0.2
  SafeHeight = 0
  StartDepth = 0
  StartVertex = 0
  StepDown = 0.2
  ToolController = -> T3__laser002
  expr: StepDown = OpToolDiameter
FEATURE [Path::FeatureCompoundPython] Operations002  # Path/CAM operation (typed FeaturePython)
  Group = -> [Engrave002]
  UsePlacements = false
FEATURE [Sketcher::SketchObject] Sketch002
  FullyConstrained = false
  sketch-geometry (19):
    g0: LineSegment StartX=-10 StartY=90 StartZ=0 EndX=90 EndY=90 EndZ=0
    g1: LineSegment StartX=90 StartY=90 StartZ=0 EndX=90 EndY=-10 EndZ=0
    g2: LineSegment StartX=90 StartY=-10 StartZ=0 EndX=-10 EndY=-10 EndZ=0
    g3: LineSegment StartX=-10 StartY=-10 StartZ=0 EndX=-10 EndY=90 EndZ=0
    g4: Circle CenterX=76 CenterY=73 CenterZ=0 NormalX=0 NormalY=0 NormalZ=1 AngleXU=0 Radius=1.2
    g5: Circle CenterX=76 CenterY=54 CenterZ=0 NormalX=0 NormalY=0 NormalZ=1 AngleXU=0 Radius=1.2
    g6: Circle CenterX=28 CenterY=47 CenterZ=0 NormalX=0 NormalY=0 NormalZ=1 AngleXU=0 Radius=1.8
    g7: Circle CenterX=13 CenterY=47 CenterZ=0 NormalX=0 NormalY=0 NormalZ=1 AngleXU=0 Radius=1.8
    g8: Circle CenterX=13 CenterY=74 CenterZ=0 NormalX=0 NormalY=0 NormalZ=1 AngleXU=0 Radius=1.8
    g9: Circle CenterX=28 CenterY=74 CenterZ=0 NormalX=0 NormalY=0 NormalZ=1 AngleXU=0 Radius=1.8
    g10: Circle CenterX=20.5 CenterY=64 CenterZ=0 NormalX=0 NormalY=0 NormalZ=1 AngleXU=0 Radius=10
    g11: LineSegment StartX=78.5 StartY=58.5 StartZ=0 EndX=73.5 EndY=58.5 EndZ=0
    g12: LineSegment StartX=73.5 StartY=58.5 StartZ=0 EndX=73.5 EndY=68.5 EndZ=0
    g13: LineSegment StartX=73.5 StartY=68.5 StartZ=0 EndX=78.5 EndY=68.5 EndZ=0
    g14: LineSegment StartX=78.5 StartY=68.5 StartZ=0 EndX=78.5 EndY=58.5 EndZ=0
    g15: Circle CenterX=-6 CenterY=86 CenterZ=0 NormalX=0 NormalY=0 NormalZ=1 AngleXU=0 Radius=1.8
    g16: Circle CenterX=86 CenterY=86 CenterZ=0 NormalX=0 NormalY=0 NormalZ=1 AngleXU=0 Radius=1.8
    g17: Circle CenterX=-6 CenterY=-6 CenterZ=0 NormalX=0 NormalY=0 NormalZ=1 AngleXU=0 Radius=1.8
    g18: Circle CenterX=86 CenterY=-6 CenterZ=0 NormalX=0 NormalY=0 NormalZ=1 AngleXU=0 Radius=1.8
  constraints (57):
    c: Coincident(g0,g1)
    c: Coincident(g1,g2)
    c: Coincident(g2,g3)
    c: Coincident(g3,g0)
    c: Horizontal(g0)
    c: Horizontal(g2)
    c: Vertical(g1)
    c: Vertical(g3)
    c: Coincident(g11,g12)
    c: Coincident(g12,g13)
    c: Coincident(g13,g14)
    c: Coincident(g14,g11)
    c: Horizontal(g11)
    c: Horizontal(g13)
    c: Vertical(g12)
    c: Vertical(g14)
    c: DistanceY(g8,g9) = 0
    c: DistanceY(g6,g7) = 0
    c: DistanceX(g9,g6) = 0
    c: Radius(g7) = 1.8
    c: Equal(g7,g6)
    c: Equal(g6,g9)
    c: Equal(g9,g8)
    c: DistanceY(g6,g9) = 27
    c: DistanceX(g7,g6) = 15
    c: Radius(g5) = 1.2
    c: Equal(g4,g5)
    c: DistanceY(g1,g1) = 100
    c: DistanceX(g0,g0) = 100
    c: DistanceX(g11,g11) = 5
    c: DistanceY(g12,g12) = 10
    c: DistanceX(g2,g-1) = 10
    c: DistanceY(g2,g-1) = 10
    c: Radius(g10) = 10
    c: DistanceX(g7,g10) = 7.5
    c: DistanceY(g10,g8) = 10
    c: DistanceX(g7,g8) = 0
    c: Radius(g15) = 1.8
    c: Equal(g15,g16)
    c: Equal(g16,g18)
    c: Equal(g18,g17)
    c: DistanceX(g2,g17) = 4
    c: DistanceY(g2,g17) = 4
    c: DistanceY(g18,g17) = 0
    c: DistanceX(g18,g1) = 4
    c: DistanceX(g18,g16) = 0
    c: DistanceY(g16,g0) = 4
    c: DistanceY(g16,g15) = 0
    c: DistanceX(g15,g17) = 0
    c: DistanceX(g-1,g7) = 13
    c: DistanceX(g5,g4) = 0
    c: DistanceY(g5,g4) = 19
    c: DistanceX(g12,g4) = 2.5
    c: DistanceY(g12,g4) = 4.5
    c: DistanceX(g17,g5) = 82
    c: DistanceY(g17,g5) = 60
    c: DistanceY(g-1,g7) = 47
FEATURE [PartDesign::Pad] Pad002
  AllowMultiFace = false
  Direction = (1,1,1)
  Length = 3
  Length2 = 100
  Profile = -> Sketch002
  Type = 0
FEATURE [PartDesign::Body] Body008  label="top plate001"
  Group = -> [Sketch002,Pad002]
  Origin = -> Origin023
  Tip = -> Pad002
FEATURE [App::DocumentObjectGroup] Tools
  Group = -> [T3__laser]
FEATURE [Path::FeaturePython] Job  label="bottom plate job"  # Path/CAM operation (typed FeaturePython)
  GeometryTolerance = 0.01
  Model = -> Model
  Operations = -> Operations
  PostProcessor = 1
  PostProcessorOutputFile = <userpath>/work/roborep/gcode
  SetupSheet = -> SetupSheet
  Stock = -> Stock
  Tools = -> Tools
FEATURE [App::DocumentObjectGroup] Tools001  label="Tools"
  Group = -> [T3__laser001]
FEATURE [Path::FeaturePython] Job001  label="top plate job"  # Path/CAM operation (typed FeaturePython)
  GeometryTolerance = 0.01
  Model = -> Model001
  Operations = -> Operations001
  PostProcessor = 1
  PostProcessorOutputFile = <userpath>/work/roborep/gcode
  SetupSheet = -> SetupSheet001
  Stock = -> Stock001
  Tools = -> Tools001
FEATURE [App::DocumentObjectGroup] Tools002  label="Tools"
  Group = -> [T3__laser002]
FEATURE [Path::FeaturePython] Job002  label="wall with socket job"  # Path/CAM operation (typed FeaturePython)
  GeometryTolerance = 0.01
  Model = -> Model002
  Operations = -> Operations002
  PostProcessor = 1
  PostProcessorOutputFile = <userpath>/work/roborep/freecad/MQsensors/wall_with_socket.gcode
  SetupSheet = -> SetupSheet002
  Stock = -> Stock002
  Tools = -> Tools002
FEATURE [App::DocumentObjectGroup] Tools003  label="Tools"
  Group = -> [T3__laser003]
FEATURE [Path::FeaturePython] Job003  label="plain wall job"  # Path/CAM operation (typed FeaturePython)
  GeometryTolerance = 0.01
  Model = -> Model003
  Operations = -> Operations003
  PostProcessor = 1
  PostProcessorOutputFile = <userpath>/work/roborep/freecad/MQsensors/wall.gcode
  SetupSheet = -> SetupSheet003
  Stock = -> Stock003
  Tools = -> Tools003
FEATURE [App::DocumentObjectGroup] Tools004  label="Tools"
  Group = -> [T3__laser004]
FEATURE [Path::FeaturePython] Job004  label="wall with micro usb job"  # Path/CAM operation (typed FeaturePython)
  GeometryTolerance = 0.01
  Model = -> Model004
  Operations = -> Operations004
  PostProcessor = 1
  PostProcessorOutputFile = <userpath>/work/roborep/freecad/MQsensors/wall_with_microusb.gcode
  SetupSheet = -> SetupSheet004
  Stock = -> Stock004
  Tools = -> Tools004
